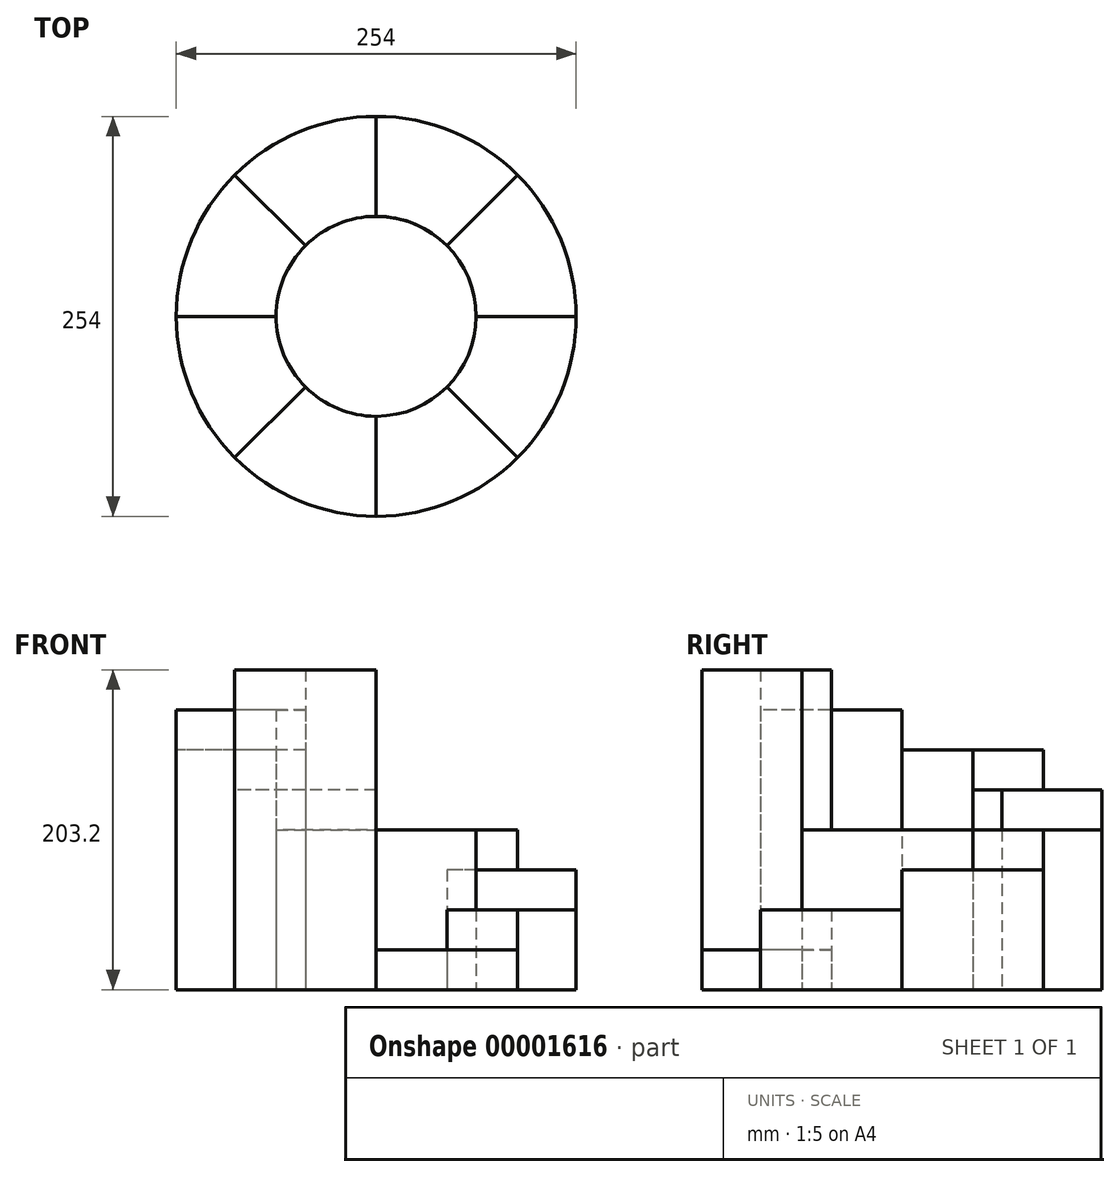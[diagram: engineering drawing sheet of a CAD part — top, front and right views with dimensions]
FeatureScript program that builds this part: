
annotation { "Feature Type Name" : "Feature", "Feature Type Description" : "" }
export const myFeature = defineFeature(function(context is Context, id is Id, definition is map)
    precondition{}
    {
        {
            var Q0;
            Q0=qCreatedBy(makeId("Top.planeOp"),FACE);
            var sketch = newSketch(context, id + "F0", { "sketchPlane" : qUnion([Q0])});
            skCircle(sketch, "E0", {"center": v(0, 0) * mm, "radius": 127 * mm});
            skCircle(sketch, "E1", {"center": v(0, 0) * mm, "radius": 63.5 * mm});
            skLineSegment(sketch, "E2", {"start": v(0, -63.5) * mm, "end": v(0, -127) * mm});
            skLineSegment(sketch, "E3", {"start": v(44.9, -44.9) * mm, "end": v(89.8, -89.8) * mm});
            skLineSegment(sketch, "E4", {"start": v(0, 63.5) * mm, "end": v(0, 127) * mm});
            skLineSegment(sketch, "E5", {"start": v(-44.9, 44.9) * mm, "end": v(-89.8, 89.8) * mm});
            skLineSegment(sketch, "E6", {"start": v(-63.5, 0) * mm, "end": v(-127, 0) * mm});
            skLineSegment(sketch, "E7", {"start": v(-44.9, -44.9) * mm, "end": v(-89.8, -89.8) * mm});
            skLineSegment(sketch, "E8", {"start": v(0, -95.25) * mm, "end": v(67.35, -67.35) * mm, "construction": true});
            skLineSegment(sketch, "E9", {"start": v(0, 95.25) * mm, "end": v(-67.35, 67.35) * mm, "construction": true});
            skLineSegment(sketch, "E10", {"start": v(-67.35, 67.35) * mm, "end": v(-95.25, 0) * mm, "construction": true});
            skLineSegment(sketch, "E11", {"start": v(-95.25, 0) * mm, "end": v(-67.35, -67.35) * mm, "construction": true});
            skLineSegment(sketch, "E12", {"start": v(-67.35, -67.35) * mm, "end": v(0, -95.25) * mm, "construction": true});
            skLineSegment(sketch, "E13", {"start": v(127, 0) * mm, "end": v(63.5, 0) * mm});
            skLineSegment(sketch, "E14", {"start": v(89.8, 89.8) * mm, "end": v(44.9, 44.9) * mm});
            skLineSegment(sketch, "E15", {"start": v(67.35, -67.35) * mm, "end": v(95.25, 0) * mm, "construction": true});
            skLineSegment(sketch, "E16", {"start": v(95.25, 0) * mm, "end": v(67.35, 67.35) * mm, "construction": true});
            skLineSegment(sketch, "E17", {"start": v(67.35, 67.35) * mm, "end": v(0, 95.25) * mm, "construction": true});
            skSolve(sketch);
        }
        {
            var Q0;
            {var subQ1=sQuery(id+"F0.wireOp",EDGE,"E2");Q0=makeQuery(id+"F0.imprint","IMPRINT",FACE,{"disambiguationData":[TD([[makeQuery(id+"F0.imprint","IMPRINT",EDGE,{"derivedFrom":subQ1}),1.0]])]});}
            extrude(context, id + "F1", {"entities" : qUnion([Q0]), "depth" : 25.4 * mm});
        }
        {
            var Q0;
            {var subQ0=sQuery(id+"F0.wireOp",EDGE,"E3");Q0=makeQuery(id+"F0.imprint","IMPRINT",FACE,{"disambiguationData":[TD([[makeQuery(id+"F0.imprint","IMPRINT",EDGE,{"derivedFrom":subQ0}),1.0]])]});}
            extrude(context, id + "F2", {"entities" : qUnion([Q0]), "depth" : 50.8 * mm});
        }
        {
            var Q0;
            {var subQ1=sQuery(id+"F0.wireOp",EDGE,"E13");Q0=makeQuery(id+"F0.imprint","IMPRINT",FACE,{"disambiguationData":[TD([[makeQuery(id+"F0.imprint","IMPRINT",EDGE,{"derivedFrom":subQ1}),-1.0]])]});}
            extrude(context, id + "F3", {"entities" : qUnion([Q0]), "depth" : 76.2 * mm});
        }
        {
            var Q0;
            {var subQ1=sQuery(id+"F0.wireOp",EDGE,"E4");Q0=makeQuery(id+"F0.imprint","IMPRINT",FACE,{"disambiguationData":[TD([[makeQuery(id+"F0.imprint","IMPRINT",EDGE,{"derivedFrom":subQ1}),-1.0]])]});}
            extrude(context, id + "F4", {"entities" : qUnion([Q0]), "depth" : 101.6 * mm});
        }
        {
            var Q0;
            {var subQ1=sQuery(id+"F0.wireOp",EDGE,"E4");Q0=makeQuery(id+"F0.imprint","IMPRINT",FACE,{"disambiguationData":[TD([[makeQuery(id+"F0.imprint","IMPRINT",EDGE,{"derivedFrom":subQ1}),1.0]])]});}
            extrude(context, id + "F5", {"entities" : qUnion([Q0]), "depth" : 127 * mm});
        }
        {
            var Q0;
            {var subQ2=sQuery(id+"F0.wireOp",EDGE,"E5");Q0=makeQuery(id+"F0.imprint","IMPRINT",FACE,{"disambiguationData":[TD([[makeQuery(id+"F0.imprint","IMPRINT",EDGE,{"derivedFrom":subQ2}),1.0]])]});}
            extrude(context, id + "F6", {"entities" : qUnion([Q0]), "depth" : 152.4 * mm});
        }
        {
            var Q0;
            {var subQ1=sQuery(id+"F0.wireOp",EDGE,"E6");Q0=makeQuery(id+"F0.imprint","IMPRINT",FACE,{"disambiguationData":[TD([[makeQuery(id+"F0.imprint","IMPRINT",EDGE,{"derivedFrom":subQ1}),1.0]])]});}
            extrude(context, id + "F7", {"entities" : qUnion([Q0]), "depth" : 177.8 * mm});
        }
        {
            var Q0;
            {var subQ1=sQuery(id+"F0.wireOp",EDGE,"E2");Q0=makeQuery(id+"F0.imprint","IMPRINT",FACE,{"disambiguationData":[TD([[makeQuery(id+"F0.imprint","IMPRINT",EDGE,{"derivedFrom":subQ1}),-1.0]])]});}
            extrude(context, id + "F8", {"entities" : qUnion([Q0]), "depth" : 203.2 * mm});
        }
        {
            var Q0;
            {var subQ0=sQuery(id+"F0.wireOp",EDGE,"E1");var subQ8=makeQuery(id+"F0.imprint","INTERSECT",VERTEX,{"derivedFrom":[subQ0,sQuery(id+"F0.wireOp",EDGE,"E13")]});Q0=makeQuery(id+"F0.imprint","IMPRINT",FACE,{"disambiguationData":[TD([[makeQuery(id+"F0.imprint","IMPRINT",EDGE,{"disambiguationData":[TD([[subQ8,-1.0]])],"derivedFrom":subQ0}),1.0]])]});}
            extrude(context, id + "F9", {"entities" : qUnion([Q0]), "depth" : 101.6 * mm});
        }
    });
